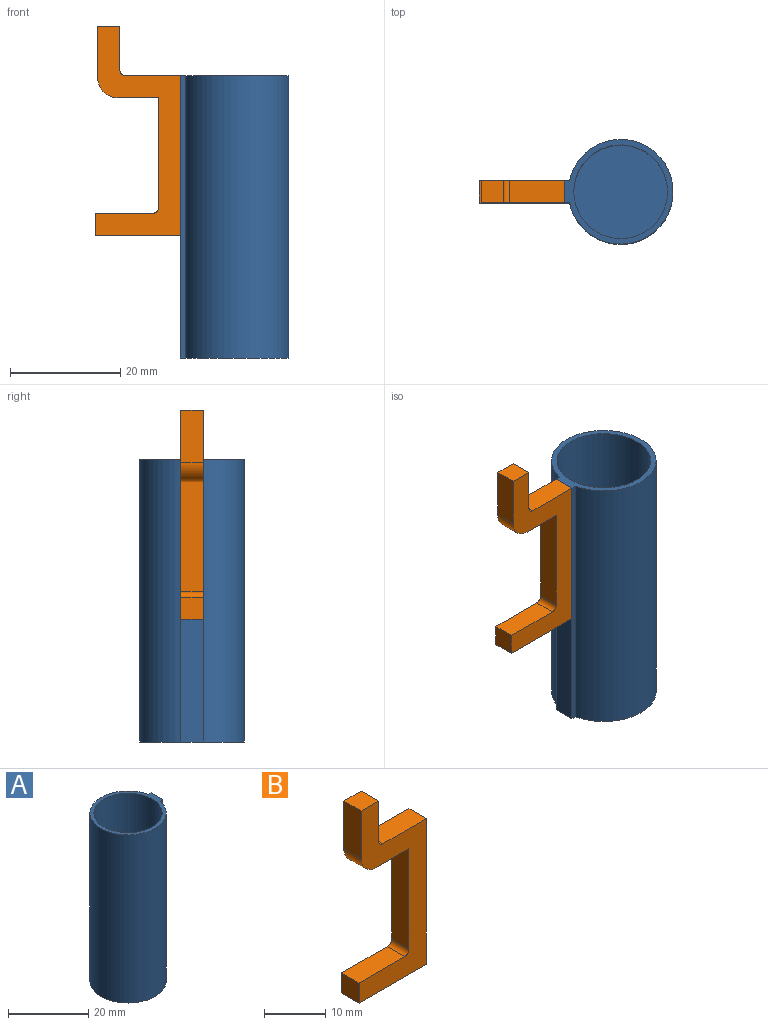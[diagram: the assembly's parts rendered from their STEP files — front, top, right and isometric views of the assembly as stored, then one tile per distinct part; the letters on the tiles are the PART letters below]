
ASSEMBLY  parts=2 mates=1
PART A: 8 faces, bbox 19.7x19x51.3 mm
  f0: plane 51.25x0.91mm, normal (0,1,0), area 46.8mm2, adj f1,f3,f5,f7
  f1: cylinder r=9.5mm len=51.25mm, axis (0,0,-1), area 2852.6mm2, adj f0,f2,f5,f7
  f2: plane 51.25x0.91mm, normal (0,-1,0), area 46.8mm2, adj f1,f3,f5,f7
  f3: plane 51.25x4mm, normal (1,0,0), area 205mm2, adj f0,f2,f5,f7
  f4: cylinder r=8.5mm len=50mm, axis (0,0,-1), area 2670.4mm2, adj f5,f6
  f5: plane 19.7x19mm, normal (0,0,1), area 59.6mm2, adj f0,f1,f2,f3,f4
  f6: plane 17x17mm, normal (0,0,1), area 227mm2, adj f4
  f7: plane 19.7x19mm, normal (0,0,-1), area 286.6mm2, adj f0,f1,f2,f3
PART B: 15 faces, bbox 15.5x4x38 mm
  f0: plane 4x4mm, normal (0,0,1), area 16mm2, adj f2,f3,f8,f10
  f1: plane 4x4mm, normal (-1,0,0), area 16mm2, adj f8,f9,f10,f11
  f2: plane 9.5x4mm, normal (-1,0,0), area 38mm2, adj f0,f8,f10,f12
  f3: plane 8x4mm, normal (1,0,0), area 32mm2, adj f0,f8,f10,f13
  f4: plane 10x4mm, normal (0,0,1), area 40mm2, adj f6,f8,f10,f13
  f5: plane 7.5x4mm, normal (0,0,-1), area 30mm2, adj f7,f8,f10,f12
  f6: plane 29x4mm, normal (1,0,0), area 116mm2, adj f4,f8,f9,f10
  f7: plane 20x4mm, normal (-1,0,0), area 80mm2, adj f5,f8,f10,f14
  f8: plane 38x15.5mm, normal (0,1,0), area 239.8mm2, adj f0,f1,f2,f3,f4,f5,f6,f7
  f9: plane 15.5x4mm, normal (0,0,-1), area 62mm2, adj f1,f6,f8,f10
  f10: plane 38x15.5mm, normal (0,-1,0), area 239.8mm2, adj f0,f1,f2,f3,f4,f5,f6,f7
  f11: plane 10.5x4mm, normal (0,0,1), area 42mm2, adj f1,f8,f10,f14
  f12: cylinder r=3.5mm len=4mm, axis (0,1,0), area 22mm2, adj f2,f5,f8,f10
  f13: cylinder r=1mm len=4mm, axis (0,1,0), area 6.3mm2, adj f3,f4,f8,f10
  f14: cylinder r=1mm len=4mm, axis (0,-1,0), area 6.3mm2, adj f7,f8,f10,f11
PLACE A rot(axis=(0,0,-1),180deg) t=(12.2,0,-23)mm
PLACE B at identity fixed
MATE fastened A.f3 <-> B.f6  axis (-1,0,0) through (2,0,27)mm
